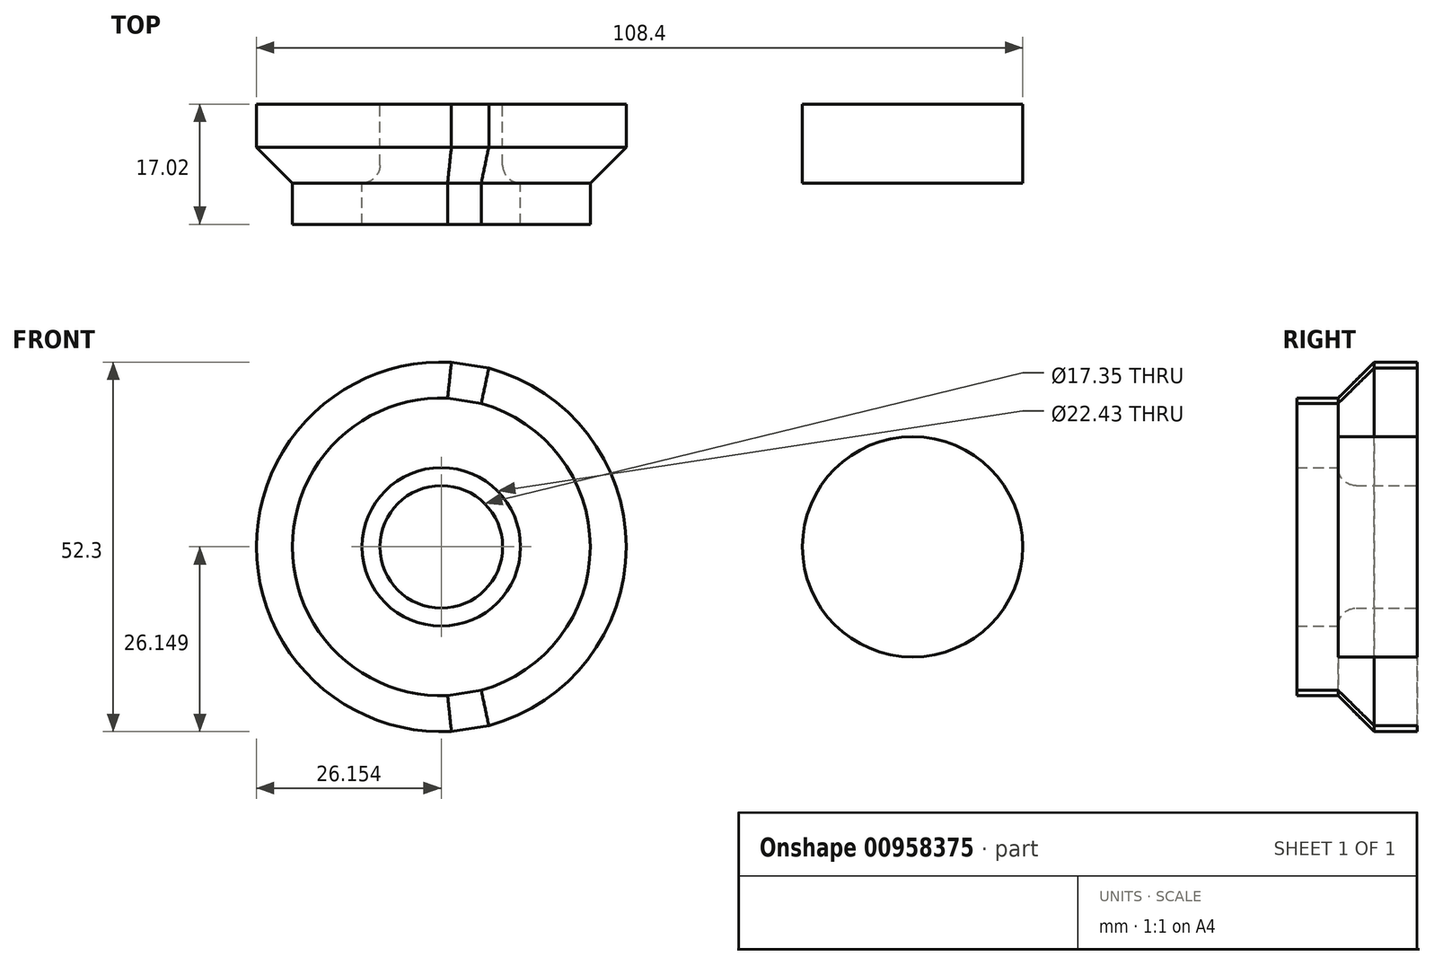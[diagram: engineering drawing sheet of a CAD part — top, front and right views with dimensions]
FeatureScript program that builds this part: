
annotation { "Feature Type Name" : "Feature", "Feature Type Description" : "" }
export const myFeature = defineFeature(function(context is Context, id is Id, definition is map)
    precondition{}
    {
        {
            var Q0;
            Q0=qCreatedBy(makeId("Front.planeOp"),FACE);
            var sketch = newSketch(context, id + "F0", { "sketchPlane" : qUnion([Q0])});
            skCircle(sketch, "E0", {"center": v(-10.43, 7.49) * mm, "radius": 8.67 * mm});
            skCircle(sketch, "E1", {"center": v(-10.43, 7.49) * mm, "radius": 26.15 * mm});
            skCircle(sketch, "E2", {"center": v(56.24, 7.49) * mm, "radius": 15.58 * mm});
            skLineSegment(sketch, "E3", {"start": v(-9, 33.6) * mm, "end": v(58.68, 22.87) * mm});
            skLineSegment(sketch, "E4", {"start": v(-9, -18.62) * mm, "end": v(58.68, -7.9) * mm});
            skSolve(sketch);
        }
        {
            var Q0;
            {var subQ0=sQuery(id+"F0.wireOp",EDGE,"E3");var subQ1=sQuery(id+"F0.wireOp",EDGE,"E1");var subQ2=makeQuery(id+"F0.imprint","INTERSECT",VERTEX,{"disambiguationData":[OD(0.0)],"derivedFrom":[subQ1,subQ0]});Q0=makeQuery(id+"F0.imprint","IMPRINT",FACE,{"disambiguationData":[TD([[makeQuery(id+"F0.imprint","IMPRINT",EDGE,{"disambiguationData":[TD([[subQ2,1.0]])],"derivedFrom":subQ1}),1.0]])]});}
            var Q1;
            {var subQ0=sQuery(id+"F0.wireOp",EDGE,"E4");var subQ1=sQuery(id+"F0.wireOp",EDGE,"E1");var subQ2=makeQuery(id+"F0.imprint","INTERSECT",VERTEX,{"disambiguationData":[OD(0.0)],"derivedFrom":[subQ1,subQ0]});Q1=makeQuery(id+"F0.imprint","IMPRINT",FACE,{"disambiguationData":[TD([[makeQuery(id+"F0.imprint","IMPRINT",EDGE,{"disambiguationData":[TD([[subQ2,-1.0]])],"derivedFrom":subQ1}),1.0]])]});}
            var Q2;
            {var subQ0=sQuery(id+"F0.wireOp",EDGE,"E3");var subQ1=sQuery(id+"F0.wireOp",EDGE,"E1");var subQ2=makeQuery(id+"F0.imprint","INTERSECT",VERTEX,{"disambiguationData":[OD(1.0)],"derivedFrom":[subQ1,subQ0]});Q2=makeQuery(id+"F0.imprint","IMPRINT",FACE,{"disambiguationData":[TD([[makeQuery(id+"F0.imprint","IMPRINT",EDGE,{"disambiguationData":[TD([[subQ2,1.0]])],"derivedFrom":subQ1}),-1.0]])]});}
            var Q3;
            {var subQ0=sQuery(id+"F0.wireOp",EDGE,"E2");var subQ1=makeQuery(id+"F0.imprint","INTERSECT",VERTEX,{"derivedFrom":[subQ0,sQuery(id+"F0.wireOp",EDGE,"E3")]});Q3=makeQuery(id+"F0.imprint","IMPRINT",FACE,{"disambiguationData":[TD([[makeQuery(id+"F0.imprint","IMPRINT",EDGE,{"disambiguationData":[TD([[subQ1,-1.0]])],"derivedFrom":subQ0}),1.0]])]});}
            var Q4;
            Q4=makeQuery(id+"F0.imprint","IMPRINT",FACE,{"disambiguationData":[TD([[makeQuery(id+"F0.imprint","IMPRINT",EDGE,{"derivedFrom":sQuery(id+"F0.wireOp",EDGE,"E0")}),-1.0]])]});
            extrude(context, id + "F1", {"entities" : qUnion([Q0, Q1, Q2, Q3, Q4]), "depth" : 11.18 * mm, "offsetDistance" : 25.4 * mm});
        }
        {
            var Q0;
            Q0=makeQuery(id+"F1.opExtrude","CAP_EDGE",EDGE,{"disambiguationData":[OSD([sQuery(id+"F0.wireOp",EDGE,"E0")])],"isStart":false});
            fillet(context, id + "F2", {"entities" : qUnion([Q0]), "radius" : 2.54 * mm, "tangentPropagation" : true, "allowEdgeOverflow" : false});
        }
        {
            var Q0;
            Q0=makeQuery(id+"F1.opExtrude","CAP_EDGE",EDGE,{"disambiguationData":[OSD([sQuery(id+"F0.wireOp",EDGE,"E4")])],"isStart":false});
            var Q1;
            Q1=makeQuery(id+"F1.opExtrude","CAP_FACE",FACE,{"disambiguationData":[OSD([sQuery(id+"F0.wireOp",EDGE,"E0"),sQuery(id+"F0.wireOp",EDGE,"E1"),sQuery(id+"F0.wireOp",EDGE,"E2"),sQuery(id+"F0.wireOp",EDGE,"E3"),sQuery(id+"F0.wireOp",EDGE,"E4")])],"isStart":false});
            chamfer(context, id + "F3", {"entities" : qUnion([Q0, Q1]), "width" : 5.08 * mm, "tangentPropagation" : true});
        }
        {
            var Q0;
            Q0=makeQuery(id+"F1.opExtrude","CAP_FACE",FACE,{"disambiguationData":[OSD([sQuery(id+"F0.wireOp",EDGE,"E0"),sQuery(id+"F0.wireOp",EDGE,"E1"),sQuery(id+"F0.wireOp",EDGE,"E2"),sQuery(id+"F0.wireOp",EDGE,"E3"),sQuery(id+"F0.wireOp",EDGE,"E4")])],"isStart":false});
            extrude(context, id + "F4", {"entities" : qUnion([Q0]), "operationType" : NewBodyOperationType.ADD, "depth" : 5.84 * mm, "offsetDistance" : 25.4 * mm});
        }
    });
